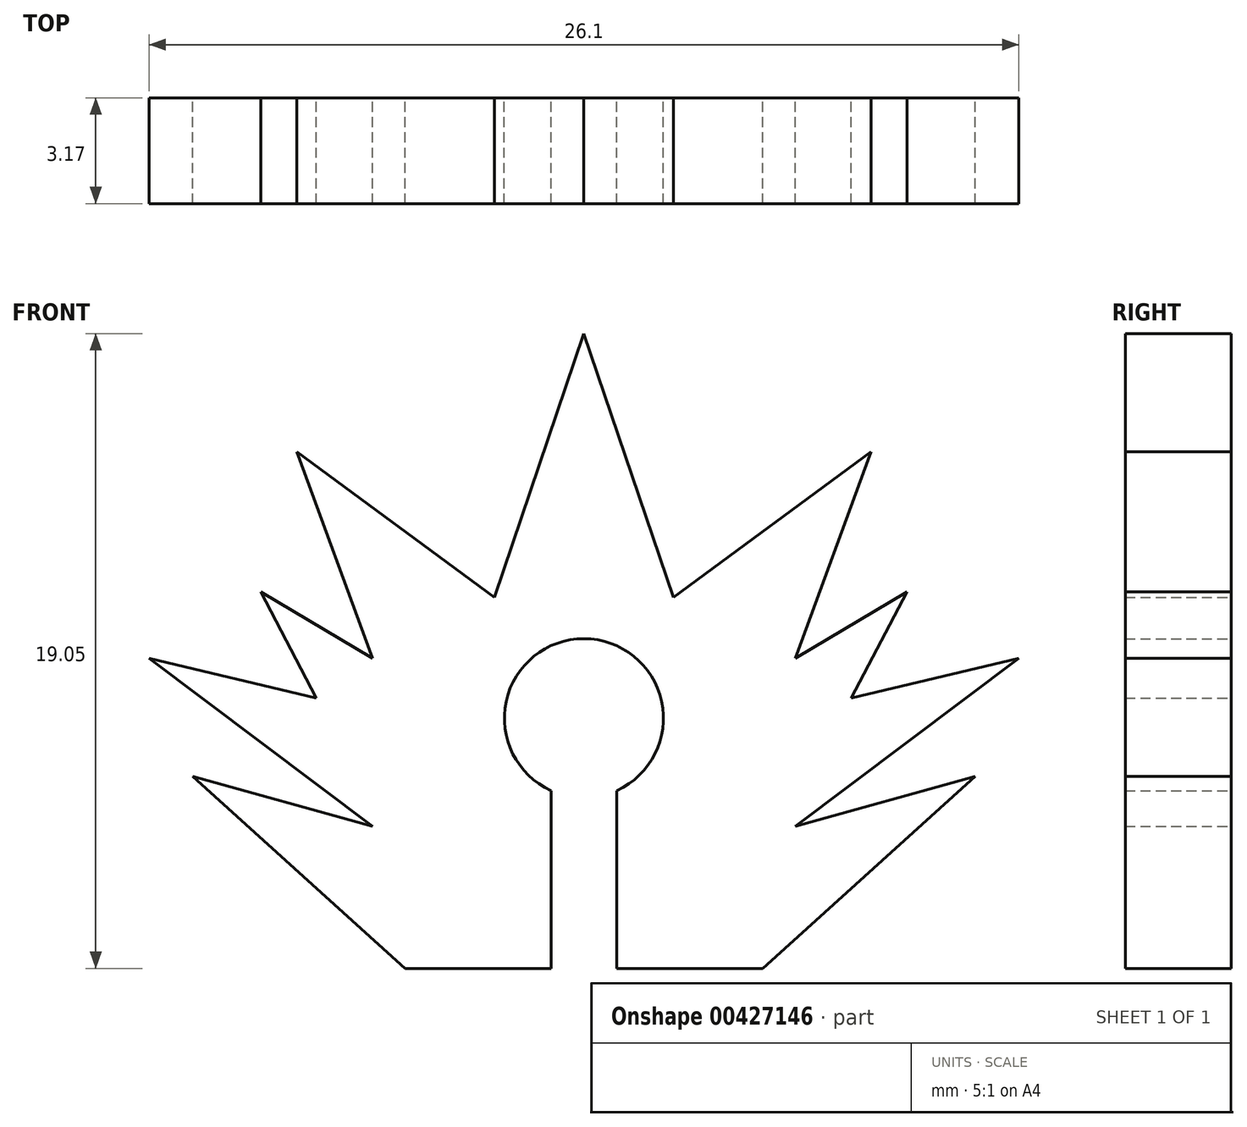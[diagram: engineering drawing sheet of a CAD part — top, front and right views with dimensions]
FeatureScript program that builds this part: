
annotation { "Feature Type Name" : "Feature", "Feature Type Description" : "" }
export const myFeature = defineFeature(function(context is Context, id is Id, definition is map)
    precondition{}
    {
        {
            var Q0;
            Q0=qCreatedBy(makeId("Front.planeOp"),FACE);
            var sketch = newSketch(context, id + "F0", { "sketchPlane" : qUnion([Q0])});
            skLineSegment(sketch, "E0", {"start": v(0, 0) * mm, "end": v(0, 19.05) * mm});
            skLineSegment(sketch, "E1", {"start": v(0, 19.05) * mm, "end": v(-2.69, 11.13) * mm});
            skLineSegment(sketch, "E2", {"start": v(-2.69, 11.13) * mm, "end": v(-8.62, 15.5) * mm});
            skLineSegment(sketch, "E3", {"start": v(-8.62, 15.5) * mm, "end": v(-6.34, 9.3) * mm});
            skLineSegment(sketch, "E4.MirrorCS", {"start": v(0, 19.05) * mm, "end": v(2.69, 11.13) * mm});
            skLineSegment(sketch, "E5.MirrorCS", {"start": v(2.69, 11.13) * mm, "end": v(8.62, 15.5) * mm});
            skLineSegment(sketch, "E6.MirrorCS", {"start": v(8.62, 15.5) * mm, "end": v(6.34, 9.3) * mm});
            skLineSegment(sketch, "E7", {"start": v(0, 0) * mm, "end": v(-0.99, 0) * mm});
            skLineSegment(sketch, "E8", {"start": v(0, 0) * mm, "end": v(0.99, 0) * mm});
            skLineSegment(sketch, "E9", {"start": v(0.99, 0) * mm, "end": v(0.99, 7.5) * mm});
            skLineSegment(sketch, "E10", {"start": v(-0.99, 0) * mm, "end": v(-0.99, 7.5) * mm});
            skLineSegment(sketch, "E11", {"start": v(-0.99, 7.5) * mm, "end": v(0.99, 7.5) * mm});
            skCircle(sketch, "E12", {"center": v(0, 7.5) * mm, "radius": 2.39 * mm});
            skLineSegment(sketch, "E13", {"start": v(-5.36, 0) * mm, "end": v(-0.99, 0) * mm});
            skLineSegment(sketch, "E14", {"start": v(0.99, 0) * mm, "end": v(5.36, 0) * mm});
            skLineSegment(sketch, "E15", {"start": v(-8.03, 8.1) * mm, "end": v(-13.05, 9.3) * mm});
            skLineSegment(sketch, "E16", {"start": v(-13.05, 9.3) * mm, "end": v(-6.34, 4.26) * mm});
            skLineSegment(sketch, "E17", {"start": v(-6.34, 4.26) * mm, "end": v(-11.74, 5.76) * mm});
            skLineSegment(sketch, "E18", {"start": v(-11.74, 5.76) * mm, "end": v(-5.36, 0) * mm});
            skLineSegment(sketch, "E19", {"start": v(-8.03, 8.1) * mm, "end": v(-9.7, 11.3) * mm});
            skPoint(sketch, "E19.endSnap0", {"position": v(-9.7, 6.78) * mm});
            skLineSegment(sketch, "E20", {"start": v(-9.7, 11.3) * mm, "end": v(-6.34, 9.3) * mm});
            skLineSegment(sketch, "E21.MirrorCS", {"start": v(9.7, 11.3) * mm, "end": v(6.34, 9.3) * mm});
            skLineSegment(sketch, "E22.MirrorCS", {"start": v(8.03, 8.1) * mm, "end": v(9.7, 11.3) * mm});
            skLineSegment(sketch, "E23.MirrorCS", {"start": v(8.03, 8.1) * mm, "end": v(13.05, 9.3) * mm});
            skLineSegment(sketch, "E24.MirrorCS", {"start": v(13.05, 9.3) * mm, "end": v(6.34, 4.26) * mm});
            skLineSegment(sketch, "E25.MirrorCS", {"start": v(6.34, 4.26) * mm, "end": v(11.74, 5.76) * mm});
            skLineSegment(sketch, "E26.MirrorCS", {"start": v(11.74, 5.76) * mm, "end": v(5.36, 0) * mm});
            skSolve(sketch);
        }
        {
            var Q0;
            {var subQ0=sQuery(id+"F0.wireOp",EDGE,"E1");Q0=makeQuery(id+"F0.imprint","IMPRINT",FACE,{"disambiguationData":[TD([[makeQuery(id+"F0.imprint","IMPRINT",EDGE,{"derivedFrom":subQ0}),1.0]])]});}
            var Q1;
            {var subQ0=sQuery(id+"F0.wireOp",EDGE,"E4.MirrorCS");Q1=makeQuery(id+"F0.imprint","IMPRINT",FACE,{"disambiguationData":[TD([[makeQuery(id+"F0.imprint","IMPRINT",EDGE,{"derivedFrom":subQ0}),-1.0]])]});}
            extrude(context, id + "F1", {"entities" : qUnion([Q0, Q1]), "depth" : 3.17 * mm});
        }
    });
